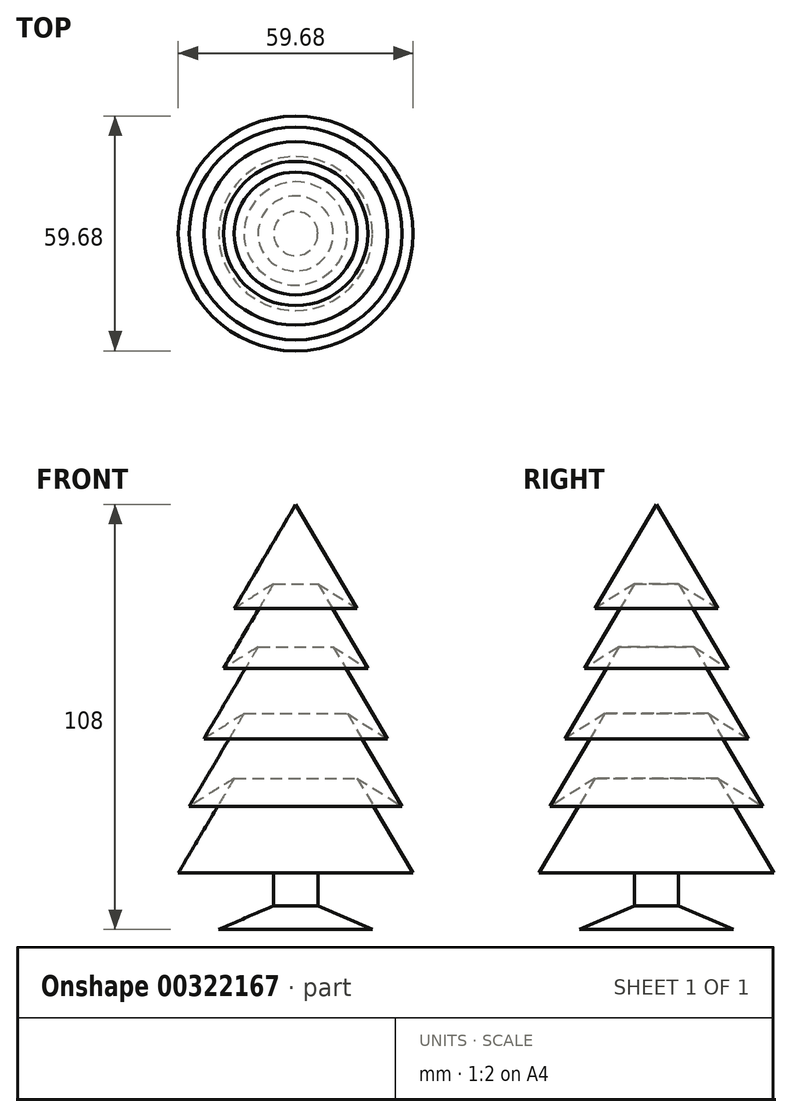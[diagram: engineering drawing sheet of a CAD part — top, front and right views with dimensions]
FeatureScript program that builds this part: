
annotation { "Feature Type Name" : "Feature", "Feature Type Description" : "" }
export const myFeature = defineFeature(function(context is Context, id is Id, definition is map)
    precondition{}
    {
        {
            var Q0;
            Q0=qCreatedBy(makeId("Front.planeOp"),FACE);
            var sketch = newSketch(context, id + "F0", { "sketchPlane" : qUnion([Q0])});
            skLineSegment(sketch, "E0", {"start": v(0, 54.83) * mm, "end": v(15.6, 28.4) * mm});
            skLineSegment(sketch, "E1", {"start": v(15.6, 28.4) * mm, "end": v(5.62, 34.65) * mm});
            skLineSegment(sketch, "E2", {"start": v(5.62, 34.65) * mm, "end": v(18.32, 13.13) * mm});
            skLineSegment(sketch, "E3", {"start": v(18.32, 13.13) * mm, "end": v(9.54, 18.62) * mm});
            skLineSegment(sketch, "E4", {"start": v(9.54, 18.62) * mm, "end": v(23.33, -4.72) * mm});
            skLineSegment(sketch, "E5", {"start": v(23.33, -4.72) * mm, "end": v(13.12, 1.66) * mm});
            skLineSegment(sketch, "E6", {"start": v(13.12, 1.66) * mm, "end": v(27.03, -21.9) * mm});
            skLineSegment(sketch, "E7", {"start": v(27.03, -21.9) * mm, "end": v(15.6, -14.75) * mm});
            skLineSegment(sketch, "E8", {"start": v(15.6, -14.75) * mm, "end": v(29.84, -38.85) * mm});
            skLineSegment(sketch, "E9", {"start": v(29.84, -38.85) * mm, "end": v(0, -38.85) * mm});
            skLineSegment(sketch, "E10", {"start": v(0, -38.85) * mm, "end": v(0, 54.83) * mm});
            skLineSegment(sketch, "E11", {"start": v(5.62, -38.85) * mm, "end": v(5.62, -47.13) * mm});
            skLineSegment(sketch, "E12", {"start": v(5.62, -47.13) * mm, "end": v(0, -47.13) * mm});
            skLineSegment(sketch, "E13", {"start": v(0, -47.13) * mm, "end": v(0, -38.85) * mm});
            skLineSegment(sketch, "E14", {"start": v(5.62, -47.13) * mm, "end": v(19.56, -53.17) * mm});
            skLineSegment(sketch, "E15", {"start": v(19.56, -53.17) * mm, "end": v(0, -53.17) * mm});
            skLineSegment(sketch, "E16", {"start": v(0, -53.17) * mm, "end": v(0, -47.13) * mm});
            skSolve(sketch);
        }
        {
            var Q0;
            Q0 = qSketchRegion(id + "F0", true);
            var Q1;
            Q1=sQuery(id+"F0.wireOp",EDGE,"E10");
            revolve(context, id + "F1", {"entities" : qUnion([Q0]), "axis" : qUnion([Q1]), "revolveType" : RevolveType.FULL});
        }
    });
